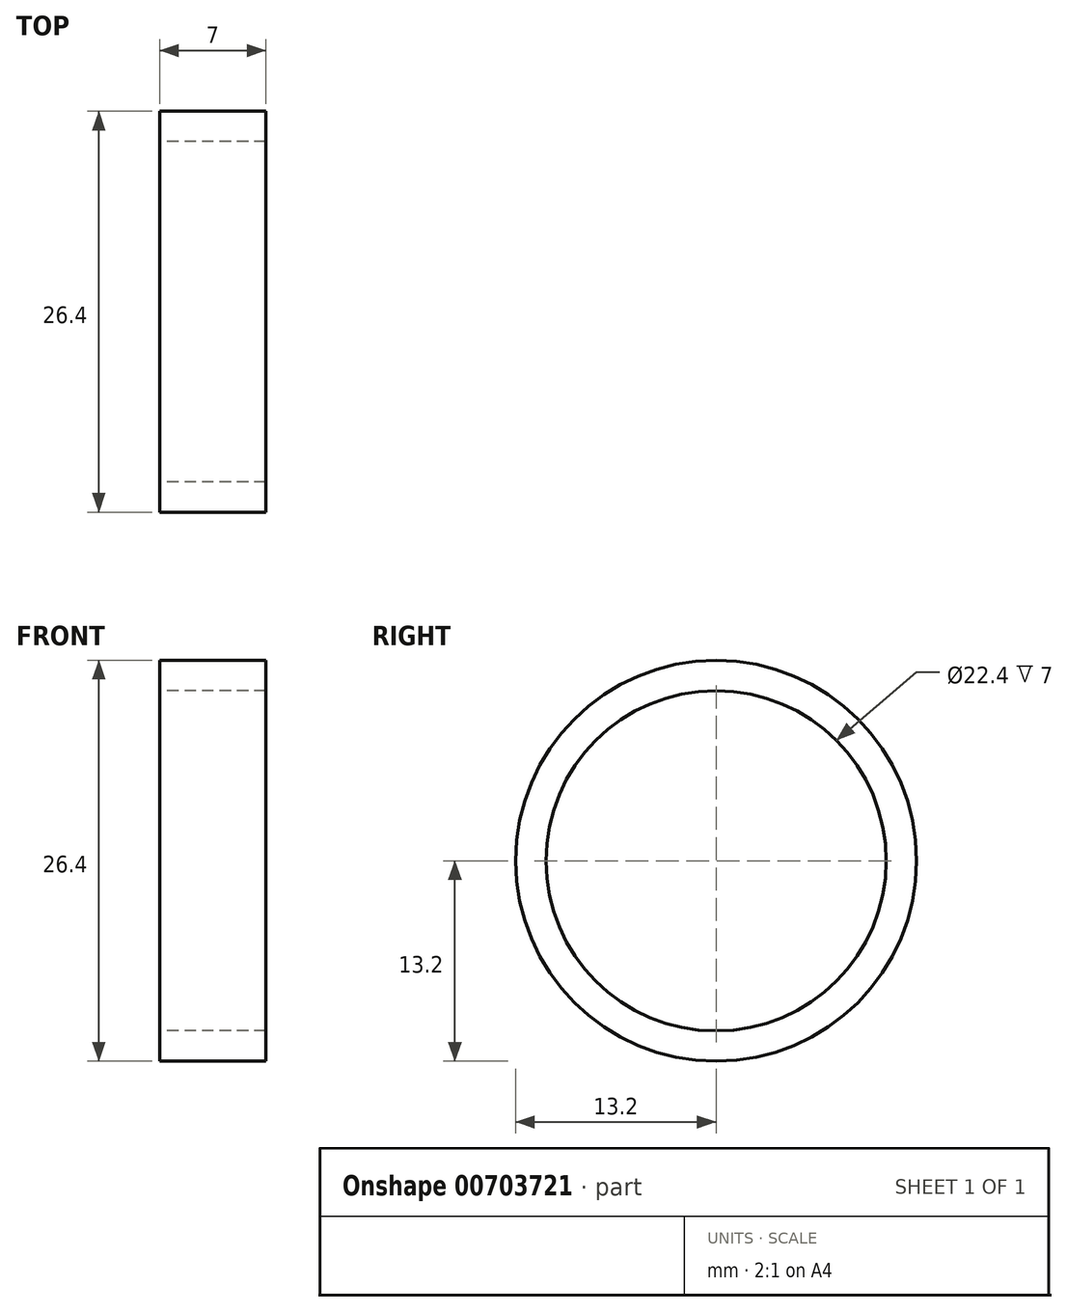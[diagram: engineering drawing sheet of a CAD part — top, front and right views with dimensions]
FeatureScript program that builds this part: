
annotation { "Feature Type Name" : "Feature", "Feature Type Description" : "" }
export const myFeature = defineFeature(function(context is Context, id is Id, definition is map)
    precondition{}
    {
        {
            var Q0;
            Q0=qCreatedBy(makeId("Right.planeOp"),FACE);
            var sketch = newSketch(context, id + "F0", { "sketchPlane" : qUnion([Q0])});
            skCircle(sketch, "E0", {"center": v(0, 0) * mm, "radius": 11.2 * mm});
            skCircle(sketch, "E1", {"center": v(0, 0) * mm, "radius": 13.2 * mm});
            skArc(sketch, "E2", {"start": v(13.2, 0) * mm, "mid": v(0, 13.18) * mm, "end": v(-13.2, 0) * mm, "construction": true});
            skArc(sketch, "E3", {"start": v(4.21, 10.38) * mm, "mid": v(0.5, 13.33) * mm, "end": v(-3.42, 10.66) * mm, "construction": true});
            skSolve(sketch);
        }
        {
            var Q0;
            Q0=makeQuery(id+"F0.imprint","IMPRINT",FACE,{"disambiguationData":[TD([[makeQuery(id+"F0.imprint","IMPRINT",EDGE,{"derivedFrom":sQuery(id+"F0.wireOp",EDGE,"E0")}),-1.0]])]});
            extrude(context, id + "F1", {"entities" : qUnion([Q0]), "depth" : 7 * mm, "offsetDistance" : 25 * mm});
        }
    });
